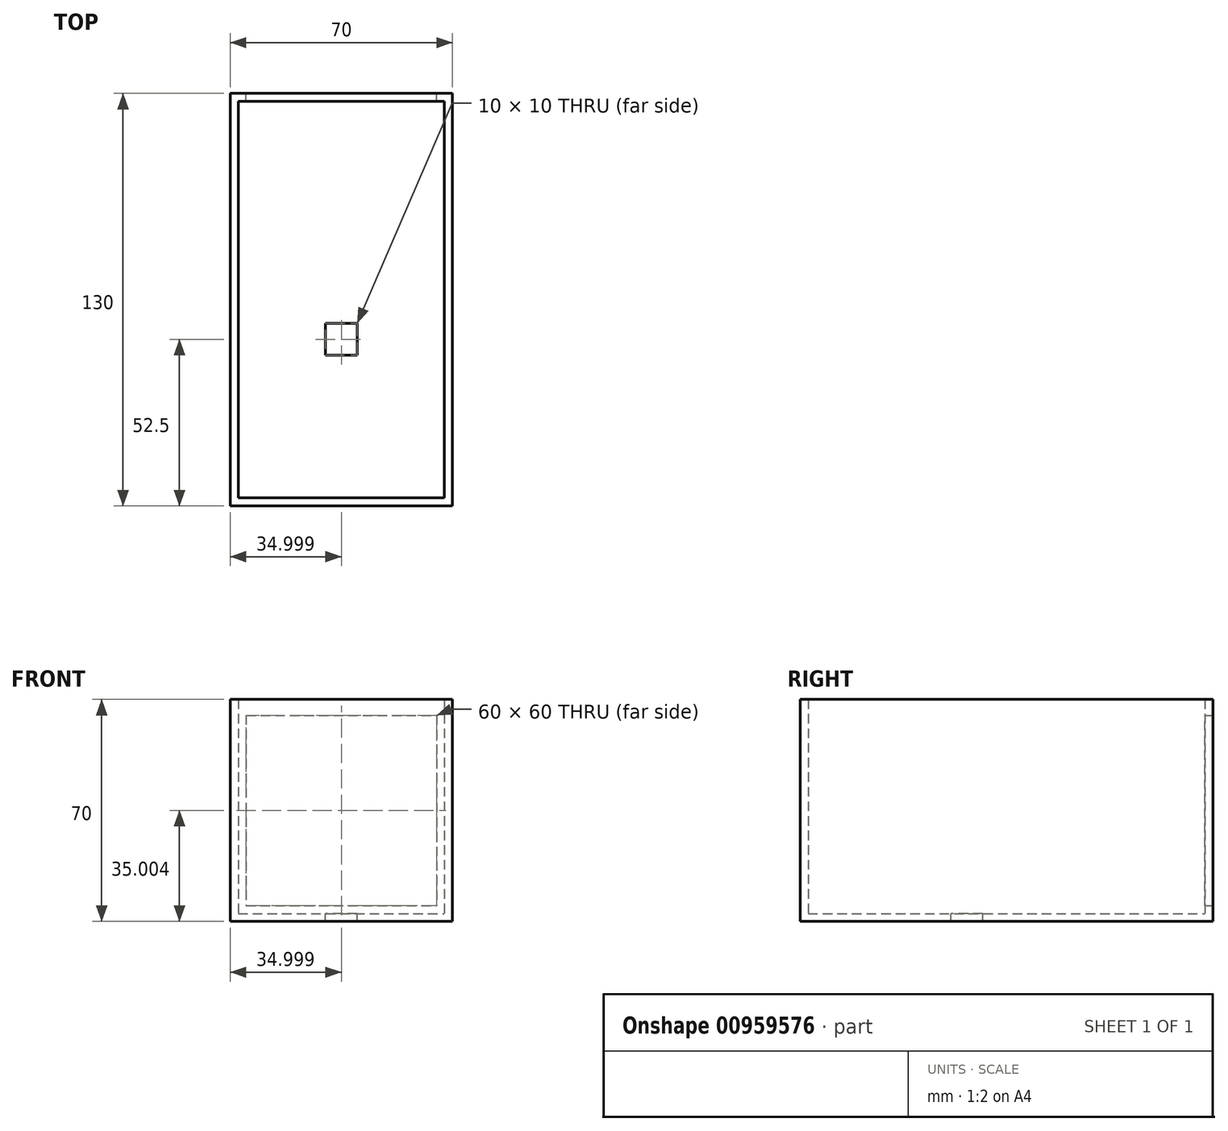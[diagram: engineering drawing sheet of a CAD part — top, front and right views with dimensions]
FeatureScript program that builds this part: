
annotation { "Feature Type Name" : "Feature", "Feature Type Description" : "" }
export const myFeature = defineFeature(function(context is Context, id is Id, definition is map)
    precondition{}
    {
        {
            var Q0;
            Q0=qCreatedBy(makeId("Front.planeOp"),FACE);
            var sketch = newSketch(context, id + "F0", { "sketchPlane" : qUnion([Q0])});
            skLineSegment(sketch, "E0.bottom", {"start": v(-41.76, 44.28) * mm, "end": v(28.24, 44.28) * mm});
            skLineSegment(sketch, "E0.top", {"start": v(-41.76, -25.72) * mm, "end": v(28.24, -25.72) * mm});
            skLineSegment(sketch, "E0.left", {"start": v(-41.76, 44.28) * mm, "end": v(-41.76, -25.72) * mm});
            skLineSegment(sketch, "E0.right", {"start": v(28.24, 44.28) * mm, "end": v(28.24, -25.72) * mm});
            skSolve(sketch);
        }
        {
            var Q0;
            Q0=makeQuery(id+"F0.imprint","IMPRINT",FACE,{"disambiguationData":[TD([[makeQuery(id+"F0.imprint","IMPRINT",EDGE,{"derivedFrom":sQuery(id+"F0.wireOp",EDGE,"E0.bottom")}),-1.0]])]});
            extrude(context, id + "F1", {"entities" : qUnion([Q0]), "depth" : 130 * mm, "offsetDistance" : 25 * mm});
        }
        {
            var Q0;
            Q0=makeQuery(id+"F1.opExtrude","SWEPT_FACE",FACE,{"disambiguationData":[OSD([sQuery(id+"F0.wireOp",EDGE,"E0.bottom")])]});
            shell(context, id + "F2", {"entities" : qUnion([Q0]), "thickness" : 2.5 * mm});
        }
        {
            var Q0;
            Q0=qCreatedBy(makeId("Front.planeOp"),FACE);
            var sketch = newSketch(context, id + "F3", { "sketchPlane" : qUnion([Q0])});
            skPoint(sketch, "E1", {"position": v(-36.76, 39.28) * mm});
            skPoint(sketch, "E2", {"position": v(23.24, 39.28) * mm});
            skPoint(sketch, "E3", {"position": v(23.24, -20.72) * mm});
            skPoint(sketch, "E4", {"position": v(-36.76, -20.72) * mm});
            skLineSegment(sketch, "E5.bottom", {"start": v(-36.76, 39.28) * mm, "end": v(23.24, 39.28) * mm});
            skLineSegment(sketch, "E5.top", {"start": v(-36.76, -20.72) * mm, "end": v(23.24, -20.72) * mm});
            skLineSegment(sketch, "E5.left", {"start": v(-36.76, 39.28) * mm, "end": v(-36.76, -20.72) * mm});
            skLineSegment(sketch, "E5.right", {"start": v(23.24, 39.28) * mm, "end": v(23.24, -20.72) * mm});
            skSolve(sketch);
        }
        {
            var Q0;
            Q0=makeQuery(id+"F3.imprint","IMPRINT",FACE,{"disambiguationData":[TD([[makeQuery(id+"F3.imprint","IMPRINT",EDGE,{"derivedFrom":sQuery(id+"F3.wireOp",EDGE,"E5.bottom")}),-1.0]])]});
            extrude(context, id + "F4", {"entities" : qUnion([Q0]), "operationType" : NewBodyOperationType.REMOVE, "depth" : 25 * mm, "offsetDistance" : 25 * mm});
        }
        {
            var Q0;
            Q0=makeQuery(id+"F2.opShell","OFFSET_FACE",FACE,{"disambiguationData":[OSD([sQuery(id+"F0.wireOp",EDGE,"E0.top")])]});
            var sketch = newSketch(context, id + "F5", { "sketchPlane" : qUnion([Q0])});
            skLineSegment(sketch, "E6.bottom", {"start": v(25.74, -2.5) * mm, "end": v(-39.26, -2.5) * mm});
            skLineSegment(sketch, "E6.top", {"start": v(25.74, -127.5) * mm, "end": v(-39.26, -127.5) * mm});
            skLineSegment(sketch, "E6.left", {"start": v(25.74, -2.5) * mm, "end": v(25.74, -127.5) * mm});
            skLineSegment(sketch, "E6.right", {"start": v(-39.26, -2.5) * mm, "end": v(-39.26, -127.5) * mm});
            skLineSegment(sketch, "E7.bottom", {"start": v(-1.76, -72.5) * mm, "end": v(-11.76, -72.5) * mm});
            skLineSegment(sketch, "E7.top", {"start": v(-1.76, -82.5) * mm, "end": v(-11.76, -82.5) * mm});
            skLineSegment(sketch, "E7.left", {"start": v(-1.76, -72.5) * mm, "end": v(-1.76, -82.5) * mm});
            skLineSegment(sketch, "E7.right", {"start": v(-11.76, -72.5) * mm, "end": v(-11.76, -82.5) * mm});
            skPoint(sketch, "E7.middle", {"position": v(-6.76, -77.5) * mm});
            skPoint(sketch, "E8.orphan", {"position": v(-6.76, -2.5) * mm});
            skPoint(sketch, "E9.orphan", {"position": v(-6.76, -127.5) * mm});
            skSolve(sketch);
        }
        {
            var Q0;
            Q0=makeQuery(id+"F5.imprint","IMPRINT",FACE,{"disambiguationData":[TD([[makeQuery(id+"F5.imprint","IMPRINT",EDGE,{"derivedFrom":sQuery(id+"F5.wireOp",EDGE,"E7.bottom")}),1.0]])]});
            extrude(context, id + "F6", {"entities" : qUnion([Q0]), "operationType" : NewBodyOperationType.REMOVE, "oppositeDirection" : true, "depth" : 25 * mm, "offsetDistance" : 25 * mm});
        }
    });
